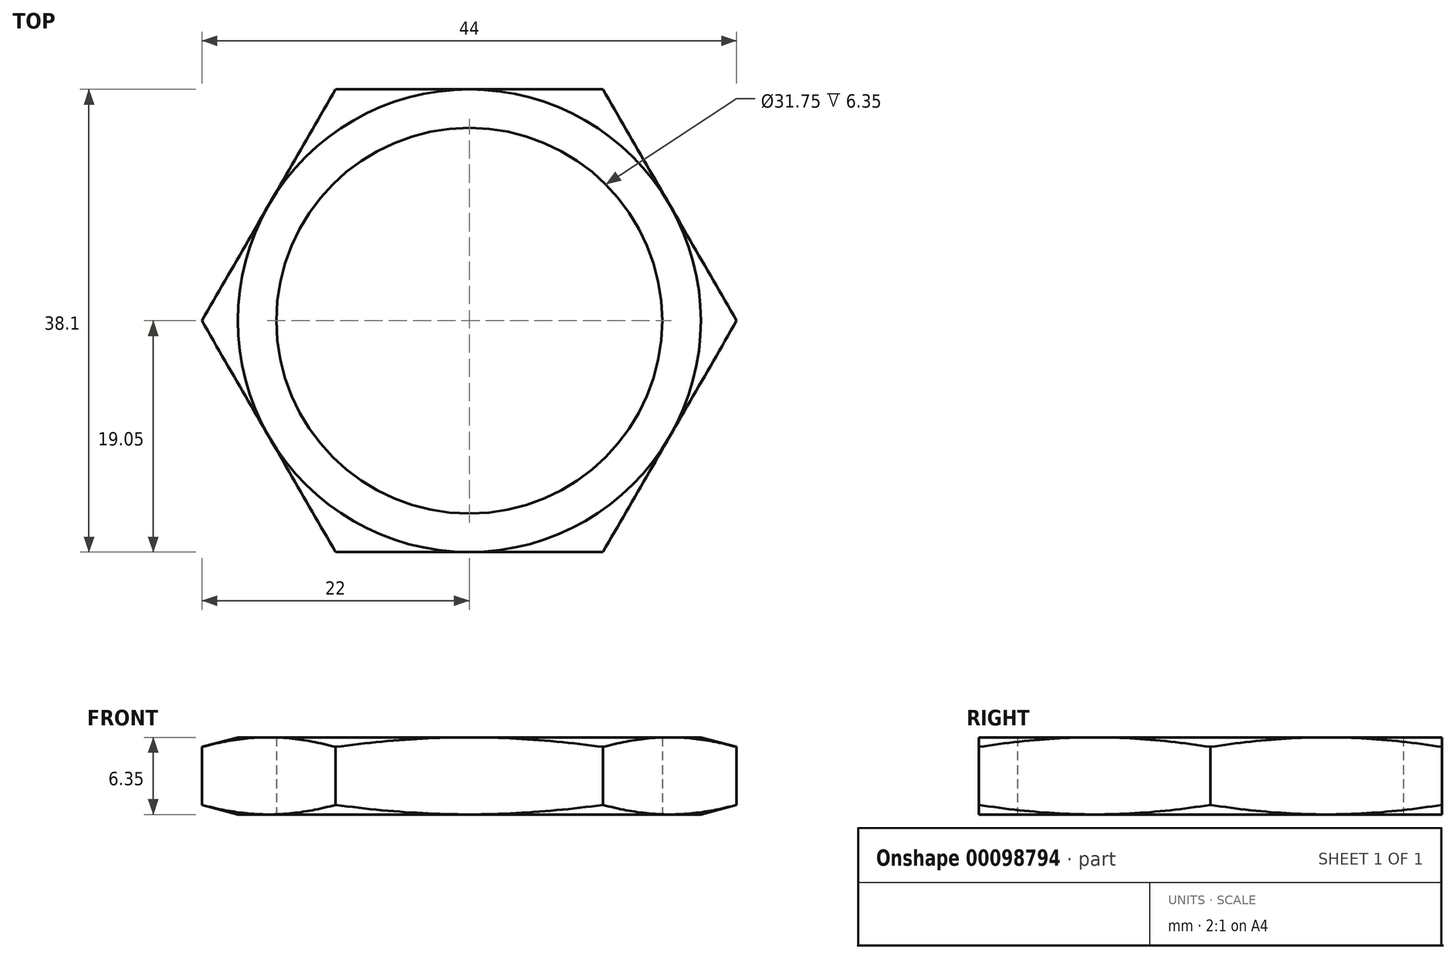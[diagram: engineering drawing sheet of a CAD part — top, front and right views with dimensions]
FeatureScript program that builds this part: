
annotation { "Feature Type Name" : "Feature", "Feature Type Description" : "" }
export const myFeature = defineFeature(function(context is Context, id is Id, definition is map)
    precondition{}
    {
        {
            var Q0;
            Q0=qCreatedBy(makeId("Top.planeOp"),FACE);
            var sketch = newSketch(context, id + "F0", { "sketchPlane" : qUnion([Q0])});
            skCircle(sketch, "E0.cCircle", {"center": v(0, 0) * mm, "radius": 19.05 * mm, "construction": true});
            skLineSegment(sketch, "E0.0", {"start": v(-11, 19.05) * mm, "end": v(11, 19.05) * mm});
            skLineSegment(sketch, "E0.1", {"start": v(11, 19.05) * mm, "end": v(22, 0) * mm});
            skLineSegment(sketch, "E0.2", {"start": v(22, 0) * mm, "end": v(11, -19.05) * mm});
            skLineSegment(sketch, "E0.3", {"start": v(11, -19.05) * mm, "end": v(-11, -19.05) * mm});
            skLineSegment(sketch, "E0.4", {"start": v(-11, -19.05) * mm, "end": v(-22, 0) * mm});
            skLineSegment(sketch, "E0.5", {"start": v(-22, 0) * mm, "end": v(-11, 19.05) * mm});
            skPoint(sketch, "E0.0.midPoint", {"position": v(0, 19.05) * mm});
            skCircle(sketch, "E1", {"center": v(0, 0) * mm, "radius": 15.88 * mm});
            skSolve(sketch);
        }
        {
            var Q0;
            Q0 = qSketchRegion(id + "F0", true);
            extrude(context, id + "F1", {"entities" : qUnion([Q0]), "depth" : 6.35 * mm});
        }
        {
            var Q0;
            Q0=qCreatedBy(makeId("Front.planeOp"),FACE);
            var sketch = newSketch(context, id + "F2", { "sketchPlane" : qUnion([Q0])});
            skLineSegment(sketch, "E2", {"start": v(-19.05, 6.35) * mm, "end": v(-30.9, 3.17) * mm});
            skLineSegment(sketch, "E3", {"start": v(-30.9, 3.17) * mm, "end": v(-19.05, 0) * mm});
            skLineSegment(sketch, "E4", {"start": v(-19.05, 0) * mm, "end": v(-29.21, 0) * mm});
            skLineSegment(sketch, "E5", {"start": v(-29.21, 0) * mm, "end": v(-29.21, 6.35) * mm});
            skLineSegment(sketch, "E6", {"start": v(-29.21, 6.35) * mm, "end": v(-19.05, 6.35) * mm});
            skLineSegment(sketch, "E7", {"start": v(-19.05, 12.05) * mm, "end": v(-19.05, 1.44) * mm});
            skSolve(sketch);
        }
        {
            var Q0;
            {var subQ1=sQuery(id+"F2.wireOp",EDGE,"E3");Q0=makeQuery(id+"F2.imprint","IMPRINT",FACE,{"disambiguationData":[TD([[makeQuery(id+"F2.imprint","IMPRINT",EDGE,{"derivedFrom":subQ1}),-1.0]])]});}
            var Q1;
            {var subQ0=sQuery(id+"F2.wireOp",EDGE,"E6");Q1=makeQuery(id+"F2.imprint","IMPRINT",FACE,{"disambiguationData":[TD([[makeQuery(id+"F2.imprint","IMPRINT",EDGE,{"derivedFrom":subQ0}),-1.0]])]});}
            var Q2;
            Q2=makeQuery(id+"F1.opExtrude","CAP_EDGE",EDGE,{"disambiguationData":[OSD([sQuery(id+"F0.wireOp",EDGE,"E1")])],"isStart":false});
            sweep(context, id + "F3", {"operationType" : NewBodyOperationType.REMOVE, "profiles" : qUnion([Q0, Q1]), "path" : qUnion([Q2])});
        }
    });
